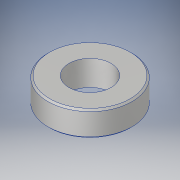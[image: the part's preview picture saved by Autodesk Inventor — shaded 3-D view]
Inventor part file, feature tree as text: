
AUTODESK INVENTOR PART (.ipt)
format: ipt  version: 2019 (Build 230136000, 136)  size: 110,080 bytes
history: native  units: mm
features: extrude x1, chamfer x1, sketch x1
ambient origin geometry x8: Origin, YZ Plane, XZ Plane, XY Plane, X Axis, Y Axis, Z Axis, Center Point
bodies: Solid1 (feature_tree)
feature tree (3):
  extrude  "Extrusion1"  Depth=5.0mm
  chamfer  "Chamfer1"  Distance=3.0mm
  sketch  "Sketch1"  dims[d0=10.0mm d1=5.0mm d2=3.0mm d3=0.0mm d4=0.2mm d5=2.0mm d6=45.0deg]
